# Revit family: Kemper - 0781G02500
name_source: partatom
category: Rohrzubehör
units: mm (PartAtom-declared; Revit-internal decimal feet)

## family parameters
Arbeitsebenenbasiert = Nein
Beim Laden mit Abzugskörper schneiden = Nein
Bemaßung runder Anschluss = Durchmesser verwenden
Gemeinsam genutzt = Nein
Immer vertikal = Ja
OmniClass-Nummer = 23.65.55.14
OmniClass-Titel = Valves for Liquid Services
Teiletyp = Ventil - Zerlegung in

## types (1)
- DN 25
    AssetType = Fixed
    Datanorm = 0781G02500
    DurationUnit = Years
    Flow = 0
    Generation ID = Kemper - 0781G02500
    Manufacturer = Kemper
    Material = stainless steel
    Model = 078 1G, SST throttle valve, with drain valve, union thread
    Modelnumber = 0781G02500
    Shape = Valve
    Size DN = 25
    Tmax, Control °C = 0
    Tmin, Control °C = 0
    WarrantyDurationUnit = Years
    collision height = 169 mm
    collision length = 168 mm
    collision volume = 168.000071607125 x 93.2000000000002 x 169.100071607125
    collision width = 93 mm
    design = pass
    kVs-Value = 0
    max. differential pressure = 1000
    perm. operating Temperature °C = 110
    perm. operating pressure Bar = 16
    productgroup = balancing valves
    sound insulation class = 1
    type = Drosselarmatur
    type of connection = male thread
    typedescription = balancing valves, 078 1G, SST throttle valve, with drain valve, union thread
    valvetype = Drosselarmatur
